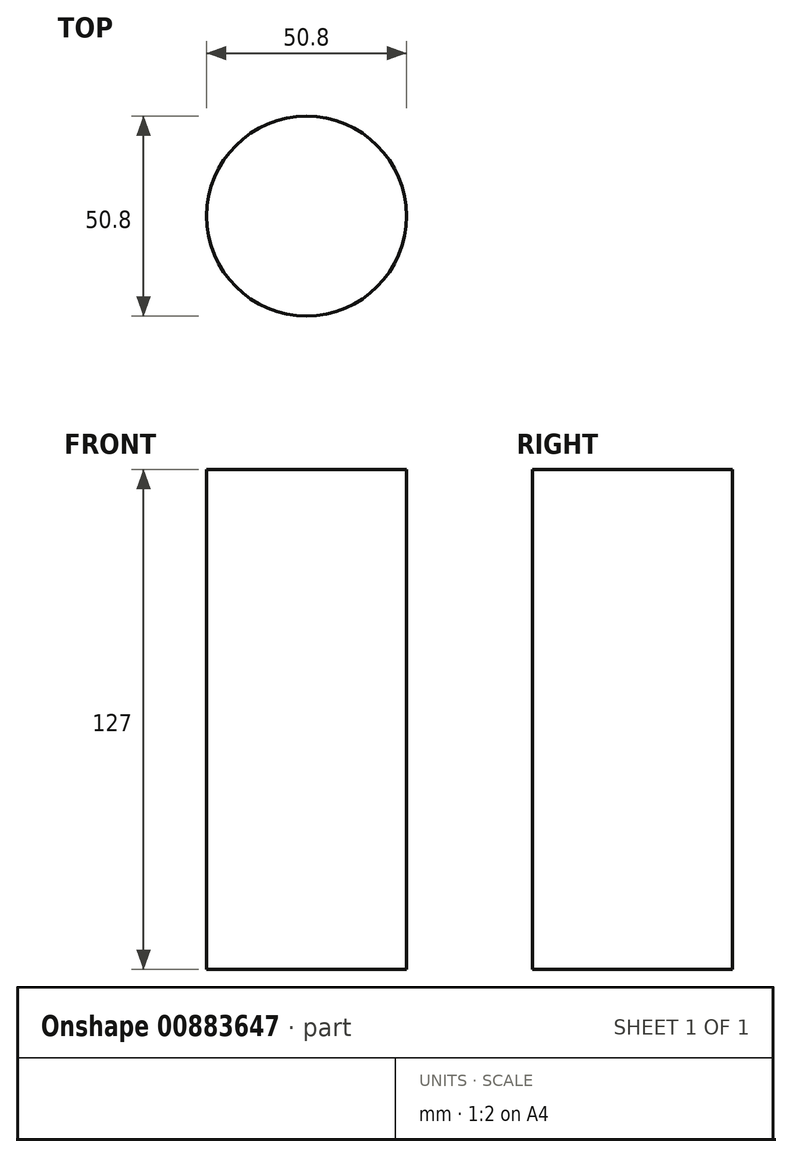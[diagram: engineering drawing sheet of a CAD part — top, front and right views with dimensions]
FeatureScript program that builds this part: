
annotation { "Feature Type Name" : "Feature", "Feature Type Description" : "" }
export const myFeature = defineFeature(function(context is Context, id is Id, definition is map)
    precondition{}
    {
        {
            var Q0;
            Q0=qCreatedBy(makeId("Top.planeOp"),FACE);
            var sketch = newSketch(context, id + "F0", { "sketchPlane" : qUnion([Q0])});
            skCircle(sketch, "E0", {"center": v(3.56, 0) * mm, "radius": 25.4 * mm});
            skSolve(sketch);
        }
        {
            var Q0;
            Q0 = qSketchRegion(id + "F0", true);
            extrude(context, id + "F1", {"entities" : qUnion([Q0]), "depth" : 127 * mm, "offsetDistance" : 25.4 * mm});
        }
    });
